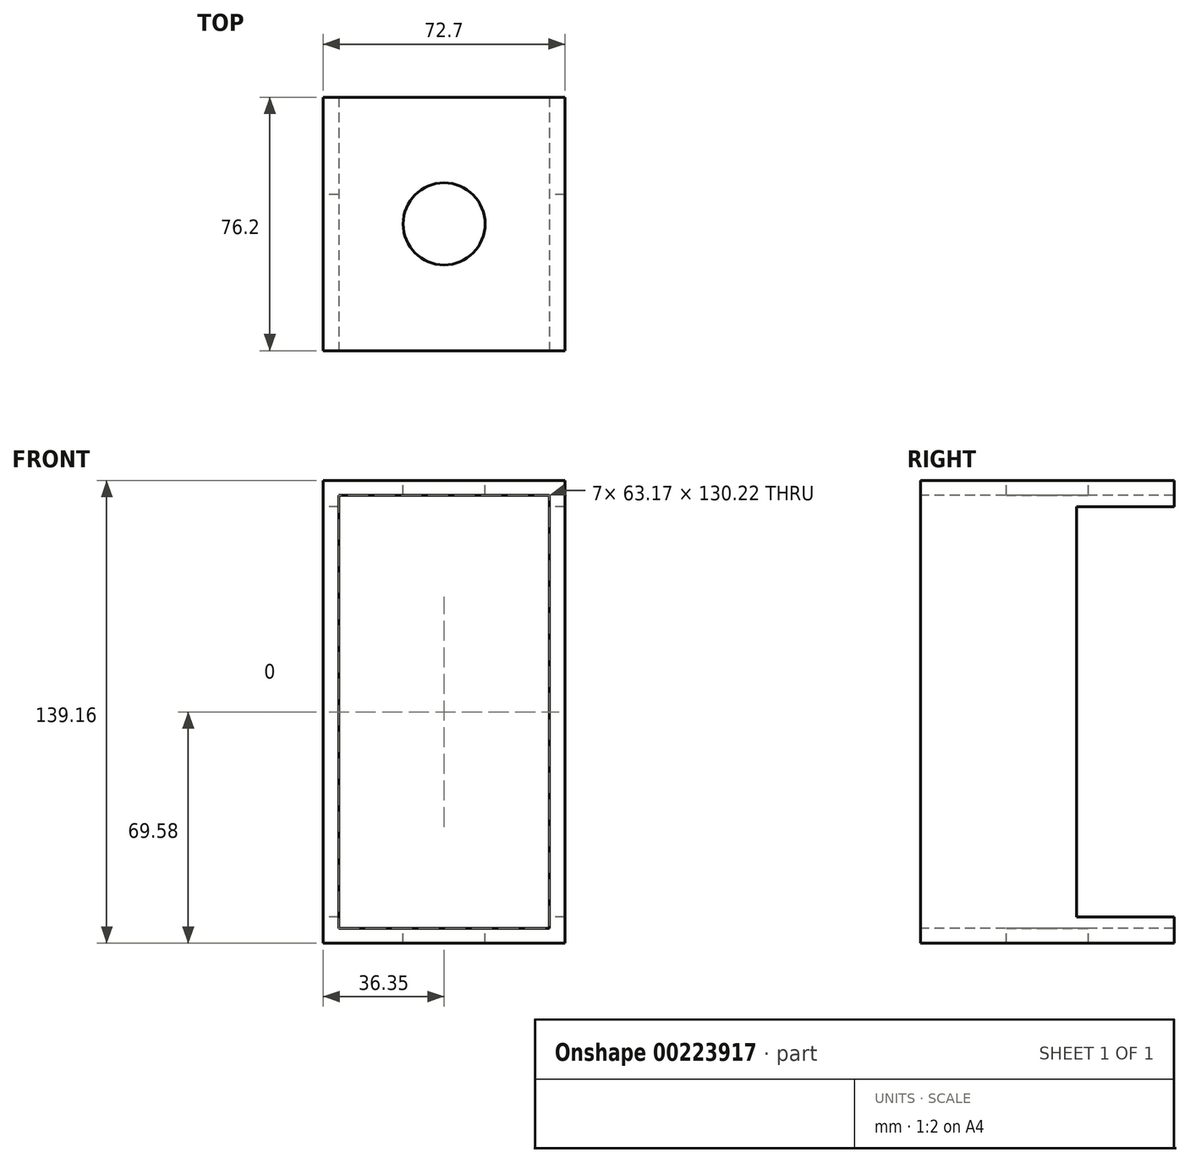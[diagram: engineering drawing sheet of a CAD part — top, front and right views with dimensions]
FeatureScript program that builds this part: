
annotation { "Feature Type Name" : "Feature", "Feature Type Description" : "" }
export const myFeature = defineFeature(function(context is Context, id is Id, definition is map)
    precondition{}
    {
        {
            var Q0;
            Q0=qCreatedBy(makeId("Front.planeOp"),FACE);
            var sketch = newSketch(context, id + "F0", { "sketchPlane" : qUnion([Q0])});
            skLineSegment(sketch, "E0.bottom", {"start": v(-36.35, 69.58) * mm, "end": v(36.35, 69.58) * mm});
            skLineSegment(sketch, "E0.top", {"start": v(-36.35, -69.58) * mm, "end": v(36.35, -69.58) * mm});
            skLineSegment(sketch, "E0.left", {"start": v(-36.35, 69.58) * mm, "end": v(-36.35, -69.58) * mm});
            skLineSegment(sketch, "E0.right", {"start": v(36.35, 69.58) * mm, "end": v(36.35, -69.58) * mm});
            skPoint(sketch, "E0.middle", {"position": v(0, 0) * mm});
            skSolve(sketch);
        }
        {
            var Q0;
            Q0 = qSketchRegion(id + "F0", true);
            extrude(context, id + "F1", {"entities" : qUnion([Q0]), "endBound" : BoundingType.SYMMETRIC, "depth" : 76.2 * mm});
        }
        {
            var Q0;
            Q0=makeQuery(id+"F1.opExtrude","CAP_FACE",FACE,{"disambiguationData":[OSD([sQuery(id+"F0.wireOp",EDGE,"E0.bottom"),sQuery(id+"F0.wireOp",EDGE,"E0.top"),sQuery(id+"F0.wireOp",EDGE,"E0.left"),sQuery(id+"F0.wireOp",EDGE,"E0.right")])],"isStart":false});
            var sketch = newSketch(context, id + "F2", { "sketchPlane" : qUnion([Q0])});
            skLineSegment(sketch, "E1.bottom", {"start": v(31.59, -65.11) * mm, "end": v(-31.59, -65.11) * mm});
            skLineSegment(sketch, "E1.top", {"start": v(31.59, 65.11) * mm, "end": v(-31.59, 65.11) * mm});
            skLineSegment(sketch, "E1.left", {"start": v(31.59, -65.11) * mm, "end": v(31.59, 65.11) * mm});
            skLineSegment(sketch, "E1.right", {"start": v(-31.59, -65.11) * mm, "end": v(-31.59, 65.11) * mm});
            skPoint(sketch, "E1.middle", {"position": v(0, 0) * mm});
            skSolve(sketch);
        }
        {
            var Q0;
            Q0=makeQuery(id+"F2.imprint","IMPRINT",FACE,{"disambiguationData":[TD([[makeQuery(id+"F2.imprint","IMPRINT",EDGE,{"derivedFrom":sQuery(id+"F2.wireOp",EDGE,"E1.bottom")}),-1.0]])]});
            extrude(context, id + "F3", {"entities" : qUnion([Q0]), "operationType" : NewBodyOperationType.REMOVE, "endBound" : BoundingType.THROUGH_ALL, "oppositeDirection" : true, "depth" : 25.4 * mm});
        }
        {
            var Q0;
            Q0=makeQuery(id+"F1.opExtrude","SWEPT_FACE",FACE,{"disambiguationData":[OSD([sQuery(id+"F0.wireOp",EDGE,"E0.bottom")])]});
            var sketch = newSketch(context, id + "F4", { "sketchPlane" : qUnion([Q0])});
            skCircle(sketch, "E2", {"center": v(0, 0) * mm, "radius": 12.33 * mm});
            skSolve(sketch);
        }
        {
            var Q0;
            Q0=makeQuery(id+"F4.imprint","IMPRINT",FACE,{"disambiguationData":[TD([[makeQuery(id+"F4.imprint","IMPRINT",EDGE,{"derivedFrom":sQuery(id+"F4.wireOp",EDGE,"E2")}),1.0]])]});
            extrude(context, id + "F5", {"entities" : qUnion([Q0]), "operationType" : NewBodyOperationType.REMOVE, "endBound" : BoundingType.THROUGH_ALL, "oppositeDirection" : true, "depth" : 25.4 * mm});
        }
        {
            var Q0;
            Q0=makeQuery(id+"F1.opExtrude","SWEPT_FACE",FACE,{"disambiguationData":[OSD([sQuery(id+"F0.wireOp",EDGE,"E0.left")])]});
            var sketch = newSketch(context, id + "F6", { "sketchPlane" : qUnion([Q0])});
            skLineSegment(sketch, "E3.bottom", {"start": v(-8.8, -61.68) * mm, "end": v(-67.4, -61.68) * mm});
            skLineSegment(sketch, "E3.top", {"start": v(-8.8, 61.68) * mm, "end": v(-67.4, 61.68) * mm});
            skLineSegment(sketch, "E3.left", {"start": v(-8.8, -61.68) * mm, "end": v(-8.8, 61.68) * mm});
            skLineSegment(sketch, "E3.right", {"start": v(-67.4, -61.68) * mm, "end": v(-67.4, 61.68) * mm});
            skPoint(sketch, "E3.middle", {"position": v(-38.1, 0) * mm});
            skSolve(sketch);
        }
        {
            var Q0;
            {var subQ0=sQuery(id+"F6.wireOp",EDGE,"E3.left");Q0=makeQuery(id+"F6.imprint","IMPRINT",FACE,{"disambiguationData":[TD([[makeQuery(id+"F6.imprint","IMPRINT",EDGE,{"derivedFrom":subQ0}),1.0]])]});}
            var Q1;
            {var subQ0=sQuery(id+"F6.wireOp",EDGE,"E3.right");Q1=makeQuery(id+"F6.imprint","IMPRINT",FACE,{"disambiguationData":[TD([[makeQuery(id+"F6.imprint","IMPRINT",EDGE,{"derivedFrom":subQ0}),-1.0]])]});}
            extrude(context, id + "F7", {"entities" : qUnion([Q0, Q1]), "operationType" : NewBodyOperationType.REMOVE, "endBound" : BoundingType.THROUGH_ALL, "oppositeDirection" : true, "depth" : 25.4 * mm});
        }
    });
